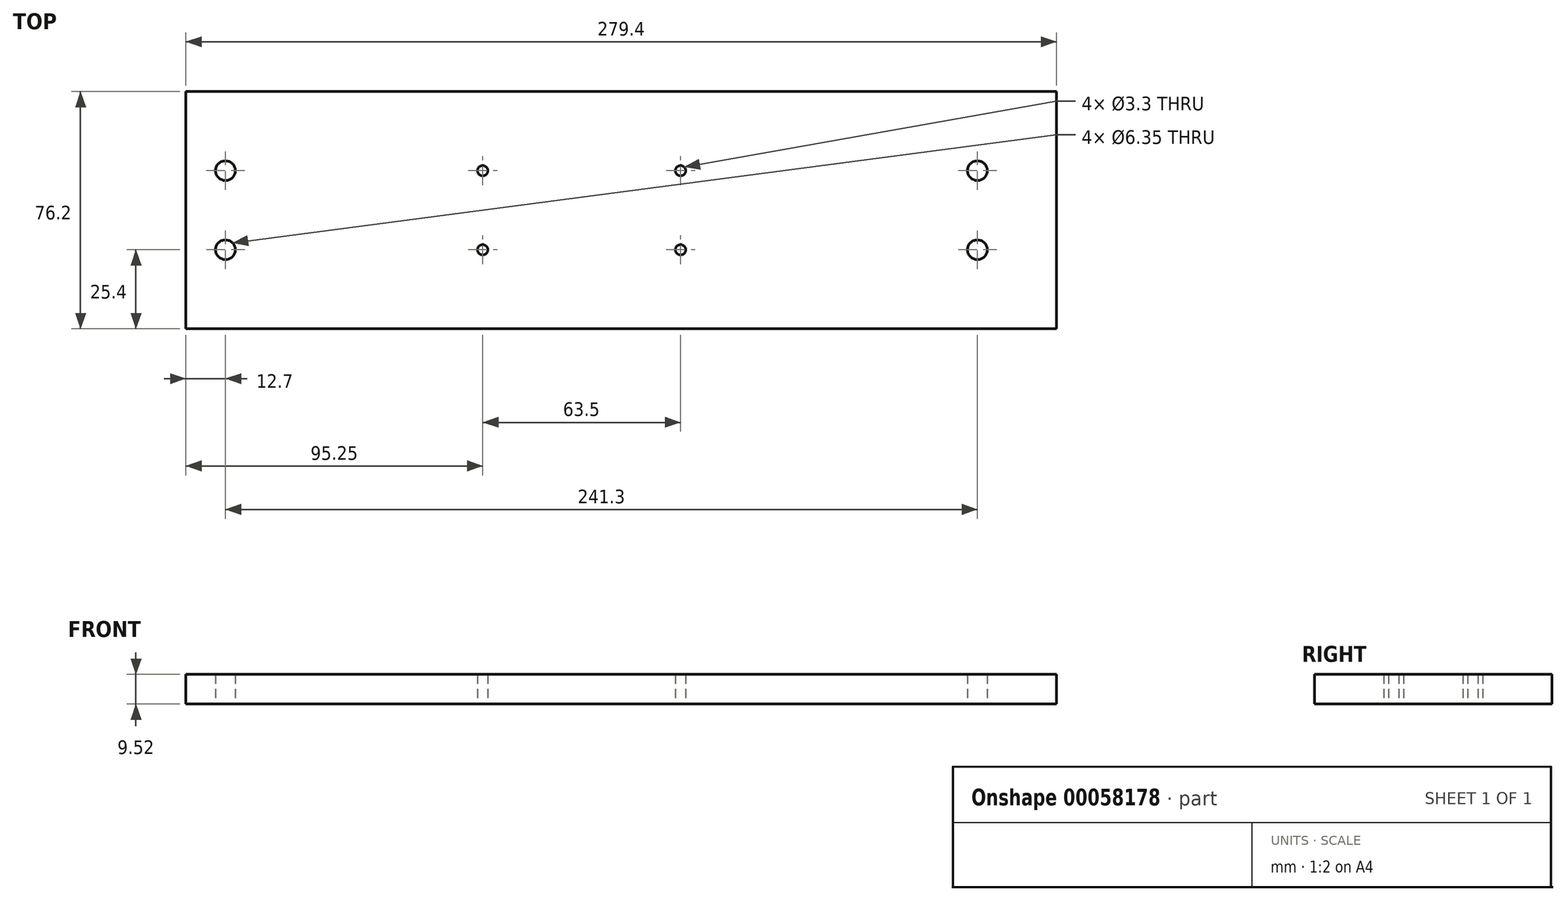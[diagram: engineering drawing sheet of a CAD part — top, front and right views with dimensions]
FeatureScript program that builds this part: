
annotation { "Feature Type Name" : "Feature", "Feature Type Description" : "" }
export const myFeature = defineFeature(function(context is Context, id is Id, definition is map)
    precondition{}
    {
        {
            var Q0;
            Q0=qCreatedBy(makeId("Top.planeOp"),FACE);
            var sketch = newSketch(context, id + "F0", { "sketchPlane" : qUnion([Q0])});
            skLineSegment(sketch, "E0.bottom", {"start": v(0, 0) * mm, "end": v(279.4, 0) * mm});
            skLineSegment(sketch, "E0.top", {"start": v(0, 76.2) * mm, "end": v(279.4, 76.2) * mm});
            skLineSegment(sketch, "E0.left", {"start": v(0, 0) * mm, "end": v(0, 76.2) * mm});
            skLineSegment(sketch, "E0.right", {"start": v(279.4, 0) * mm, "end": v(279.4, 76.2) * mm});
            skCircle(sketch, "E1", {"center": v(12.7, 50.8) * mm, "radius": 3.18 * mm});
            skCircle(sketch, "E2", {"center": v(12.7, 25.4) * mm, "radius": 3.18 * mm});
            skLineSegment(sketch, "E3", {"start": v(0, 38.1) * mm, "end": v(279.4, 38.1) * mm});
            skCircle(sketch, "E4", {"center": v(95.25, 50.8) * mm, "radius": 1.65 * mm});
            skCircle(sketch, "E5", {"center": v(95.25, 25.4) * mm, "radius": 1.65 * mm});
            skCircle(sketch, "E6", {"center": v(158.75, 50.8) * mm, "radius": 1.65 * mm});
            skCircle(sketch, "E7", {"center": v(158.75, 25.4) * mm, "radius": 1.65 * mm});
            skCircle(sketch, "E8", {"center": v(254, 50.8) * mm, "radius": 3.18 * mm});
            skCircle(sketch, "E9", {"center": v(254, 25.4) * mm, "radius": 3.18 * mm});
            skSolve(sketch);
        }
        {
            var Q0;
            Q0 = qSketchRegion(id + "F0", true);
            var Q1;
            {var subQ1=sQuery(id+"F0.wireOp",EDGE,"E0.top");Q1=makeQuery(id+"F0.imprint","IMPRINT",FACE,{"disambiguationData":[TD([[makeQuery(id+"F0.imprint","IMPRINT",EDGE,{"derivedFrom":subQ1}),-1.0]])]});}
            extrude(context, id + "F1", {"entities" : qUnion([Q0, Q1]), "endBound" : BoundingType.SYMMETRIC, "depth" : 9.52 * mm});
        }
    });
